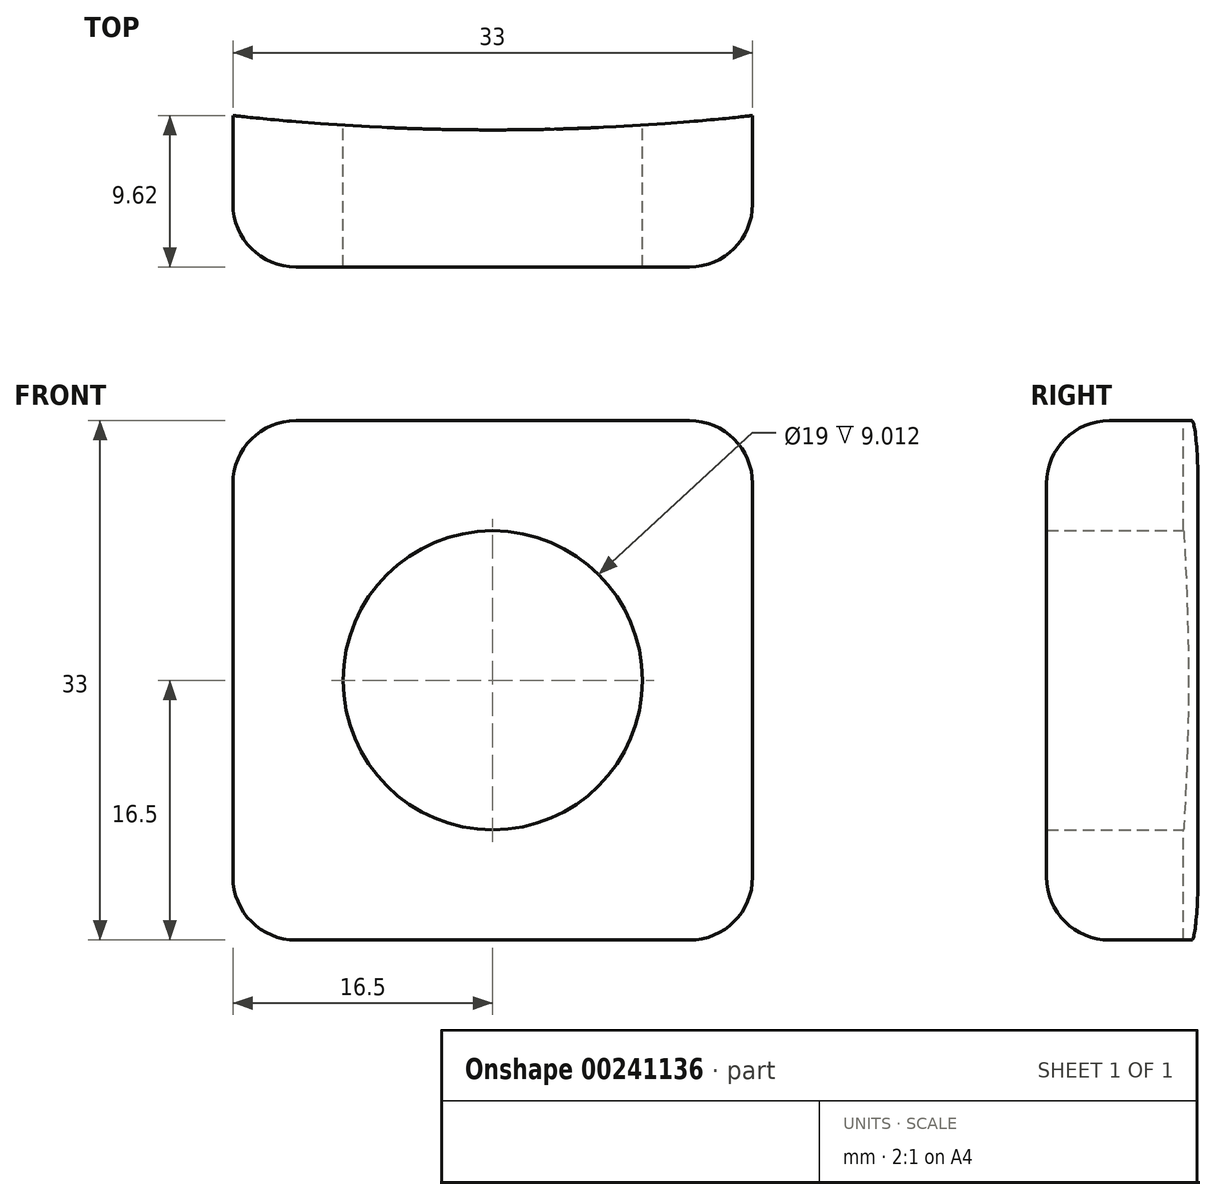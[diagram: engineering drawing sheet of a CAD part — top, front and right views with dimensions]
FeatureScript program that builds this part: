
annotation { "Feature Type Name" : "Feature", "Feature Type Description" : "" }
export const myFeature = defineFeature(function(context is Context, id is Id, definition is map)
    precondition{}
    {
        {
            var Q0;
            Q0=qCreatedBy(makeId("Front.planeOp"),FACE);
            var sketch = newSketch(context, id + "F0", { "sketchPlane" : qUnion([Q0])});
            skLineSegment(sketch, "E0.bottom", {"start": v(-16.5, 16.5) * mm, "end": v(16.5, 16.5) * mm});
            skLineSegment(sketch, "E0.top", {"start": v(-16.5, -16.5) * mm, "end": v(16.5, -16.5) * mm});
            skLineSegment(sketch, "E0.left", {"start": v(-16.5, 16.5) * mm, "end": v(-16.5, -16.5) * mm});
            skLineSegment(sketch, "E0.right", {"start": v(16.5, 16.5) * mm, "end": v(16.5, -16.5) * mm});
            skPoint(sketch, "E0.middle", {"position": v(0, 0) * mm});
            skCircle(sketch, "E1", {"center": v(0, 0) * mm, "radius": 9.5 * mm});
            skSolve(sketch);
        }
        {
            var Q0;
            Q0 = qSketchRegion(id + "F0", true);
            extrude(context, id + "F1", {"entities" : qUnion([Q0]), "depth" : 10 * mm, "offsetDistance" : 25 * mm});
        }
        {
            var Q0;
            Q0=makeQuery(id+"F1.opExtrude","CAP_EDGE",EDGE,{"disambiguationData":[OSD([sQuery(id+"F0.wireOp",EDGE,"E0.bottom")])],"isStart":false});
            var Q1;
            Q1=makeQuery(id+"F1.opExtrude","CAP_EDGE",EDGE,{"disambiguationData":[OSD([sQuery(id+"F0.wireOp",EDGE,"E0.right")])],"isStart":false});
            var Q2;
            Q2=makeQuery(id+"F1.opExtrude","CAP_EDGE",EDGE,{"disambiguationData":[OSD([sQuery(id+"F0.wireOp",EDGE,"E0.left")])],"isStart":false});
            var Q3;
            Q3=makeQuery(id+"F1.opExtrude","CAP_EDGE",EDGE,{"disambiguationData":[OSD([sQuery(id+"F0.wireOp",EDGE,"E0.top")])],"isStart":false});
            var Q4;
            Q4=makeQuery(id+"F1.opExtrude","SWEPT_EDGE",EDGE,{"disambiguationData":[OSD([sQuery(id+"F0.wireOp",EDGE,"E0.bottom"),sQuery(id+"F0.wireOp",EDGE,"E0.left")])]});
            var Q5;
            Q5=makeQuery(id+"F1.opExtrude","SWEPT_EDGE",EDGE,{"disambiguationData":[OSD([sQuery(id+"F0.wireOp",EDGE,"E0.bottom"),sQuery(id+"F0.wireOp",EDGE,"E0.right")])]});
            var Q6;
            Q6=makeQuery(id+"F1.opExtrude","SWEPT_EDGE",EDGE,{"disambiguationData":[OSD([sQuery(id+"F0.wireOp",EDGE,"E0.top"),sQuery(id+"F0.wireOp",EDGE,"E0.right")])]});
            var Q7;
            Q7=makeQuery(id+"F1.opExtrude","SWEPT_EDGE",EDGE,{"disambiguationData":[OSD([sQuery(id+"F0.wireOp",EDGE,"E0.top"),sQuery(id+"F0.wireOp",EDGE,"E0.left")])]});
            fillet(context, id + "F2", {"entities" : qUnion([Q0, Q1, Q2, Q3, Q4, Q5, Q6, Q7]), "radius" : 4 * mm, "tangentPropagation" : true, "allowEdgeOverflow" : false});
        }
        {
            var Q0;
            Q0=makeQuery(id+"F1.opExtrude","SWEPT_FACE",FACE,{"disambiguationData":[OSD([sQuery(id+"F0.wireOp",EDGE,"E0.bottom")])]});
            var sketch = newSketch(context, id + "F3", { "sketchPlane" : qUnion([Q0])});
            skCircle(sketch, "E2", {"center": v(0, 148.71) * mm, "radius": 150 * mm});
            skSolve(sketch);
        }
        {
            var Q0;
            {var subQ1=sQuery(id+"F0.wireOp",EDGE,"E0.bottom");var subQ7=makeQuery(id+"F1.opExtrude","CAP_EDGE",EDGE,{"disambiguationData":[OSD([subQ1])],"isStart":true});Q0=makeQuery(id+"F3.imprint","IMPRINT",FACE,{"disambiguationData":[TD([[makeQuery(id+"F3.imprint","IMPRINT",EDGE,{"derivedFrom":subQ7}),1.0]])]});}
            var Q1;
            {var subQ1=sQuery(id+"F0.wireOp",EDGE,"E0.bottom");var subQ7=makeQuery(id+"F1.opExtrude","CAP_EDGE",EDGE,{"disambiguationData":[OSD([subQ1])],"isStart":true});Q1=makeQuery(id+"F3.imprint","IMPRINT",FACE,{"disambiguationData":[TD([[makeQuery(id+"F3.imprint","IMPRINT",EDGE,{"derivedFrom":subQ7}),-1.0]])]});}
            extrude(context, id + "F4", {"entities" : qUnion([Q0, Q1]), "operationType" : NewBodyOperationType.REMOVE, "oppositeDirection" : true, "depth" : 500 * mm, "offsetDistance" : 25 * mm});
        }
    });
